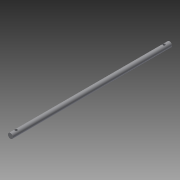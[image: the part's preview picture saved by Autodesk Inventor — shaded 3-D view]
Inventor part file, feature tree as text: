
AUTODESK INVENTOR PART (.ipt)
format: ipt  version: 2015 (Build 190159000, 159)  size: 82,944 bytes
history: native  units: in
note: dims shown in document units (in); Inventor stores cm internally (conversion verified against a paired STEP export)
features: sketch x1, revolve x1, extrude x1
ambient origin geometry x8: Origin, YZ Plane, XZ Plane, XY Plane, X Axis, Y Axis, Z Axis, Center Point
bodies: Solid1 (feature_tree)
feature tree (3):
  sketch  "Sketch1"  dims[d0=7.874in d1=0.248in d2=0.2756in d3=0.2756in d4=0.1181in d5=0.1181in d6=90.0deg d7=0.3937in d8=0.0in]
  revolve  "Revolution1"  [1 undecoded]
  extrude  "Extrusion1"  Depth=0.3937in
note: 1 required parameter value undecoded (feature->parameter linkage not recoverable at this tier; creation-order binding heuristic only, values carry confidence <= 0.55)
